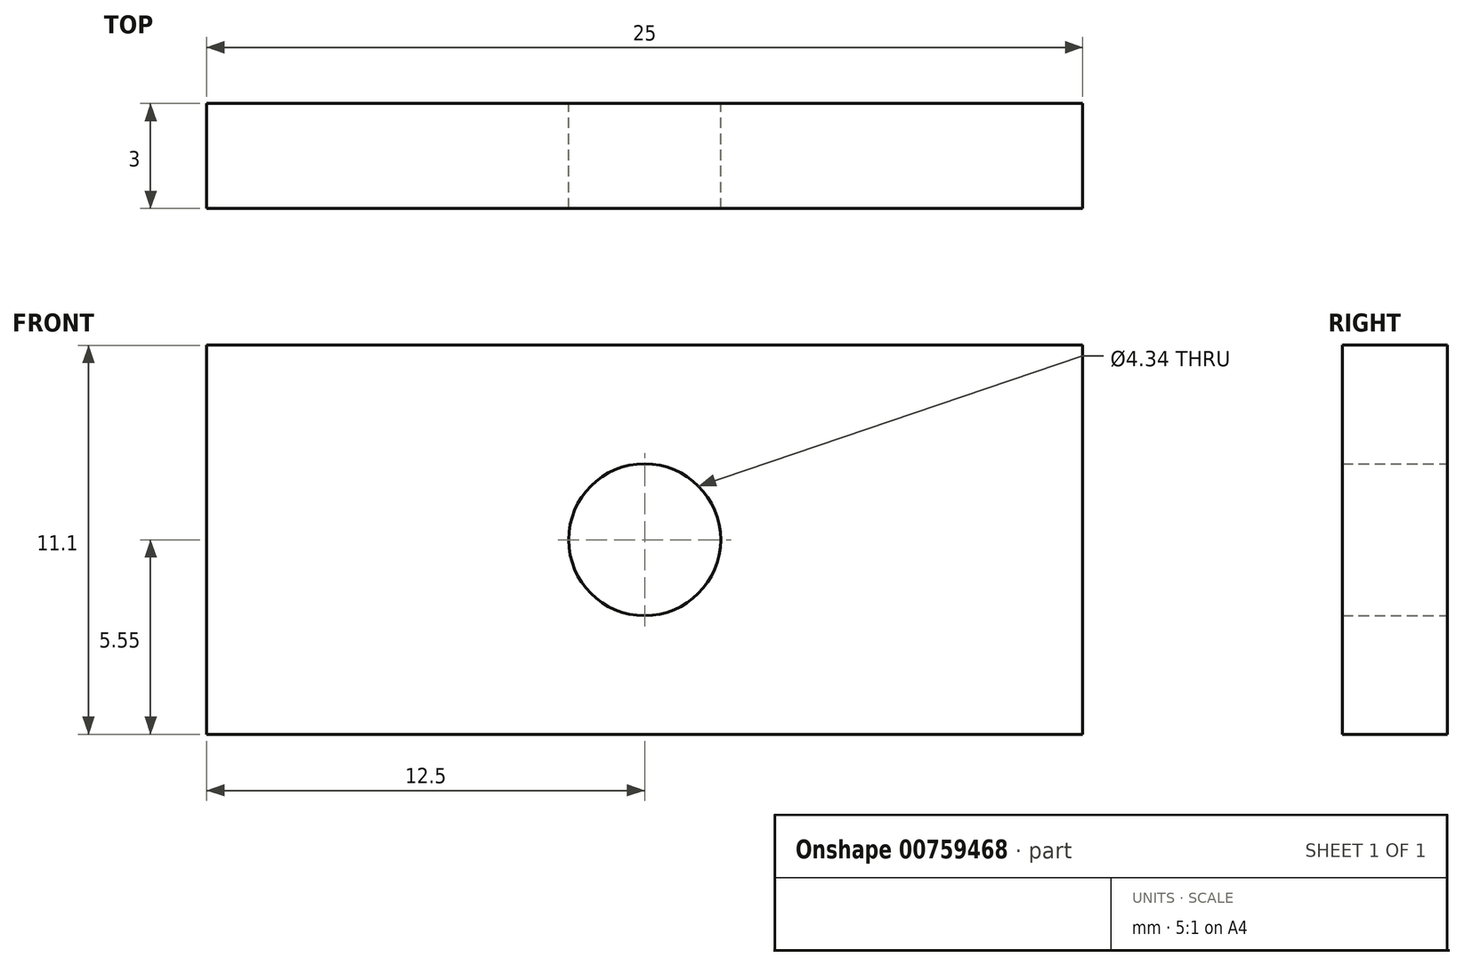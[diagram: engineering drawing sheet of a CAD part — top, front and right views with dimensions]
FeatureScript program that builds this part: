
annotation { "Feature Type Name" : "Feature", "Feature Type Description" : "" }
export const myFeature = defineFeature(function(context is Context, id is Id, definition is map)
    precondition{}
    {
        {
            var Q0;
            Q0=qCreatedBy(makeId("Front.planeOp"),FACE);
            var sketch = newSketch(context, id + "F0", { "sketchPlane" : qUnion([Q0])});
            skLineSegment(sketch, "E0.bottom", {"start": v(-12.5, 5.55) * mm, "end": v(12.5, 5.55) * mm});
            skLineSegment(sketch, "E0.top", {"start": v(-12.5, -5.55) * mm, "end": v(12.5, -5.55) * mm});
            skLineSegment(sketch, "E0.left", {"start": v(-12.5, 5.55) * mm, "end": v(-12.5, -5.55) * mm});
            skLineSegment(sketch, "E0.right", {"start": v(12.5, 5.55) * mm, "end": v(12.5, -5.55) * mm});
            skPoint(sketch, "E0.middle", {"position": v(0, 0) * mm});
            skCircle(sketch, "E1", {"center": v(0, 0) * mm, "radius": 2.17 * mm});
            skSolve(sketch);
        }
        {
            var Q0;
            Q0=makeQuery(id+"F0.imprint","IMPRINT",FACE,{"disambiguationData":[TD([[makeQuery(id+"F0.imprint","IMPRINT",EDGE,{"derivedFrom":sQuery(id+"F0.wireOp",EDGE,"E0.bottom")}),-1.0]])]});
            extrude(context, id + "F1", {"entities" : qUnion([Q0]), "depth" : 3 * mm, "offsetDistance" : 25 * mm});
        }
    });
